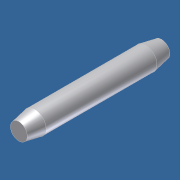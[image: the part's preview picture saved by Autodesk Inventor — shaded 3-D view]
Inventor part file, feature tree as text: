
AUTODESK INVENTOR PART (.ipt)
format: ipt  version: 2012 (Build 160160000, 160)  size: 79,360 bytes
history: native  units: in
note: dims shown in document units (in); Inventor stores cm internally (conversion verified against a paired STEP export)
features: chamfer x2, extrude x1, sketch x1
ambient origin geometry x8: Origin, YZ Plane, XZ Plane, XY Plane, X Axis, Y Axis, Z Axis, Center Point
bodies: Solid1 (feature_tree)
feature tree (4):
  extrude  "Extrusion1"  Depth=9.0in TaperAngle=0.0deg
  chamfer  "Chamfer1"  Distance=1.0in Angle=45.0deg
  chamfer  "Chamfer2"  Distance=1.0in Angle=45.0deg
  sketch  "Sketch1"  dims[d0=1.4375in d1=9.0in d2=0.0in d3=1.0in d4=0.1875in d5=45.0deg d6=1.0in d7=0.1875in d8=45.0deg]
